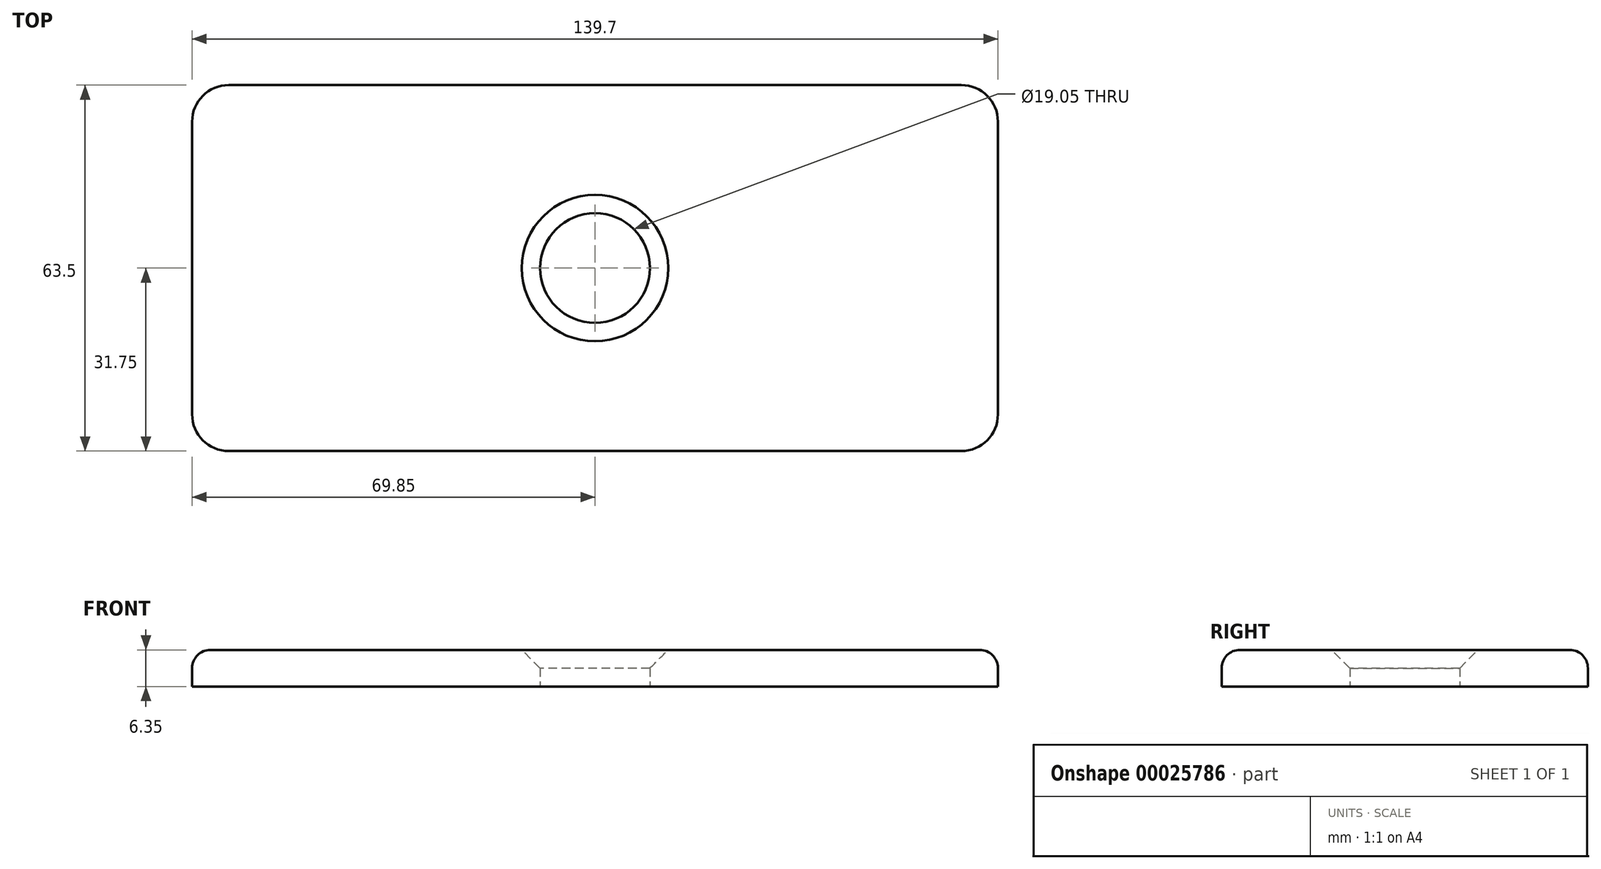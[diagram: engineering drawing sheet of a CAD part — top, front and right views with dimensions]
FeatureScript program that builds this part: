
annotation { "Feature Type Name" : "Feature", "Feature Type Description" : "" }
export const myFeature = defineFeature(function(context is Context, id is Id, definition is map)
    precondition{}
    {
        {
            var Q0;
            Q0=qCreatedBy(makeId("Top.planeOp"),FACE);
            var sketch = newSketch(context, id + "F0", { "sketchPlane" : qUnion([Q0])});
            skLineSegment(sketch, "E0.rect.bottom", {"start": v(-63.5, 31.75) * mm, "end": v(63.5, 31.75) * mm});
            skLineSegment(sketch, "E0.rect.top", {"start": v(-63.5, -31.75) * mm, "end": v(63.5, -31.75) * mm});
            skLineSegment(sketch, "E0.rect.left", {"start": v(-69.85, 25.4) * mm, "end": v(-69.85, -25.4) * mm});
            skLineSegment(sketch, "E0.rect.right", {"start": v(69.85, 25.4) * mm, "end": v(69.85, -25.4) * mm});
            skPoint(sketch, "E0.rect.middle", {"position": v(0, 0) * mm});
            skCircle(sketch, "E1", {"center": v(0, 0) * mm, "radius": 9.53 * mm});
            skPoint(sketch, "E2.visualSharp", {"position": v(-69.85, 31.75) * mm});
            skArc(sketch, "E2.filletArc", {"start": v(-63.5, 31.75) * mm, "mid": v(-68, 29.9) * mm, "end": v(-69.85, 25.4) * mm});
            skPoint(sketch, "E3.visualSharp", {"position": v(-69.85, -31.75) * mm});
            skArc(sketch, "E3.filletArc", {"start": v(-69.85, -25.4) * mm, "mid": v(-68, -29.9) * mm, "end": v(-63.5, -31.75) * mm});
            skPoint(sketch, "E4.visualSharp", {"position": v(69.85, -31.75) * mm});
            skArc(sketch, "E4.filletArc", {"start": v(63.5, -31.75) * mm, "mid": v(68, -29.9) * mm, "end": v(69.85, -25.4) * mm});
            skPoint(sketch, "E5.visualSharp", {"position": v(69.85, 31.75) * mm});
            skArc(sketch, "E5.filletArc", {"start": v(69.85, 25.4) * mm, "mid": v(68, 29.9) * mm, "end": v(63.5, 31.75) * mm});
            skSolve(sketch);
        }
        {
            var Q0;
            Q0=makeQuery(id+"F0.imprint","IMPRINT",FACE,{"disambiguationData":[TD([[makeQuery(id+"F0.imprint","IMPRINT",EDGE,{"derivedFrom":sQuery(id+"F0.wireOp",EDGE,"E0.rect.bottom")}),-1.0]])]});
            extrude(context, id + "F1", {"entities" : qUnion([Q0]), "depth" : 6.35 * mm});
        }
        {
            var Q0;
            Q0=makeQuery(id+"F1.opExtrude","CAP_EDGE",EDGE,{"disambiguationData":[OSD([sQuery(id+"F0.wireOp",EDGE,"E1")])],"isStart":false});
            chamfer(context, id + "F2", {"entities" : qUnion([Q0]), "width" : 3.17 * mm, "tangentPropagation" : true});
        }
        {
            var Q0;
            Q0=makeQuery(id+"F1.opExtrude","CAP_EDGE",EDGE,{"disambiguationData":[OSD([sQuery(id+"F0.wireOp",EDGE,"E0.rect.top")])],"isStart":false});
            var Q1;
            Q1=makeQuery(id+"F1.opExtrude","CAP_EDGE",EDGE,{"disambiguationData":[OSD([sQuery(id+"F0.wireOp",EDGE,"E0.rect.left")])],"isStart":false});
            var Q2;
            Q2=makeQuery(id+"F1.opExtrude","CAP_EDGE",EDGE,{"disambiguationData":[OSD([sQuery(id+"F0.wireOp",EDGE,"E0.rect.bottom")])],"isStart":false});
            var Q3;
            Q3=makeQuery(id+"F1.opExtrude","CAP_EDGE",EDGE,{"disambiguationData":[OSD([sQuery(id+"F0.wireOp",EDGE,"E0.rect.right")])],"isStart":false});
            fillet(context, id + "F3", {"entities" : qUnion([Q0, Q1, Q2, Q3]), "radius" : 3.17 * mm, "tangentPropagation" : true, "allowEdgeOverflow" : false});
        }
    });
